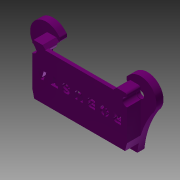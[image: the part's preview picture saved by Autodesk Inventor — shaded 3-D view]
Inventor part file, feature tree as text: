
AUTODESK INVENTOR PART (.ipt)
format: ipt  version: 2015 (Build 190159000, 159)  size: 620,032 bytes
history: native  units: mm
features: sketch x11, extrude x11, projected_geometry x5, plane x3
ambient origin geometry x8: Origin, YZ Plane, XZ Plane, XY Plane, X Axis, Y Axis, Z Axis, Center Point
bodies: Body1 (feature_tree)
feature tree (30):
  plane  "Work Plane2"
  sketch  "Sketch12"  dims[d19=46.65mm d72=0.0mm d125=-8.5mm d129=3.5mm]
  plane  "Work Plane3"
  extrude  "Extrusion9"  Depth=3.5mm
  extrude  "Extrusion10"  Depth=7.0mm TaperAngle=0.0deg
  extrude  "Extrusion11"  Depth=3.5mm TaperAngle=0.0deg
  extrude  "Extrusion12"  Depth=3.5mm TaperAngle=0.0deg
  extrude  "Extrusion13"  Depth=3.5mm TaperAngle=0.0deg
  extrude  "Extrusion14"  Depth=4.46mm
  extrude  "Extrusion15"  Depth=50.0mm TaperAngle=0.0deg
  plane  "Work Plane4"
  extrude  "Extrusion16"  Depth=7.1mm
  extrude  "Extrusion17"  Depth=7.1mm
  extrude  "Extrusion18"  Depth=50.0mm
  extrude  "Extrusion19"  [1 undecoded]
  sketch  "Sketch13"  dims[d136=-5.0mm d137=7.0mm d138=0.0mm]
  sketch  "Sketch14"  dims[d139=3.5mm d140=0.0mm d143=13.5mm d144=0.0mm]
  sketch  "Sketch16"  dims[d145=3.5mm d146=0.0mm d147=3.5mm d148=0.0mm]
  projected_geometry  "Projected Loop1"
  projected_geometry  "Projected Loop2"
  projected_geometry  "Projected Loop3"
  sketch  "Sketch17"  dims[d149=3.5mm d150=0.0mm d158=3.5mm d159=0.0mm]
  sketch  "Sketch18"  dims[d161=0.0mm d162=4.46mm]
  projected_geometry  "Projected Loop4"
  sketch  "Sketch19"  dims[d163=45.0deg d164=50.0mm d165=0.0mm]
  projected_geometry  "Projected Loop6"
  sketch  "Sketch20"  dims[d166=7.1mm d167=7.1mm]
  sketch  "Sketch21"  dims[d168=0.0mm d169=0.0mm d170=7.1mm]
  sketch  "Sketch22"  dims[d171=50.0mm d172=0.0mm d173=7.1mm]
  sketch  "Sketch25"  dims[d174=50.0mm d175=0.0mm]
note: 1 required parameter value undecoded (feature->parameter linkage not recoverable at this tier; creation-order binding heuristic only, values carry confidence <= 0.55)
